# Revit family: R1900
name_source: partatom
category: Pipe Accessories
revit_build: Autodesk Revit 2018 (Build: 20170223_1515(x64)
units: mm (PartAtom-declared; Revit-internal decimal feet)

## family parameters
Always vertical = Yes
Cut with Voids When Loaded = No
Part Type = Normal
Round Connector Dimension = Use Diameter
Shared = No
Work Plane-Based = No

## types (5) — shared parameters
Description = VERTICAL EXPANSION JOINT
Floor Drain Material = Paint - Sherwin Williams Paint - #952C2A - Bellwood Red
Manufacturer = MIFAB
Model = R1900
URL = WWW.MIFAB.COM

## per-type parameters (varying)
| type | Height | Pipe Diameter | Pipe Radius |
| R1902_2" Dai_Vertical Expansion Joint | 0' - 7" | 0' - 2" | 0' - 1" |
| R1903_3" Dai_Vertical Expansion Joint | 0' - 8" | 0' - 3" | 0' - 1 1/2" |
| R1904_4" Dai_Vertical Expansion Joint | 0' - 8 1/2" | 0' - 4" | 0' - 2" |
| R1906_6" Dai_Vertical Expansion Joint | 0' - 8 1/2" | 0' - 6" | 0' - 3" |
| R1908_8" Dai_Vertical Expansion Joint | 0' - 11" | 0' - 8" | 0' - 4" |

## geometry (parser evidence)
native form markers: Sweep x7
no freeform markers — native parametric forms only
